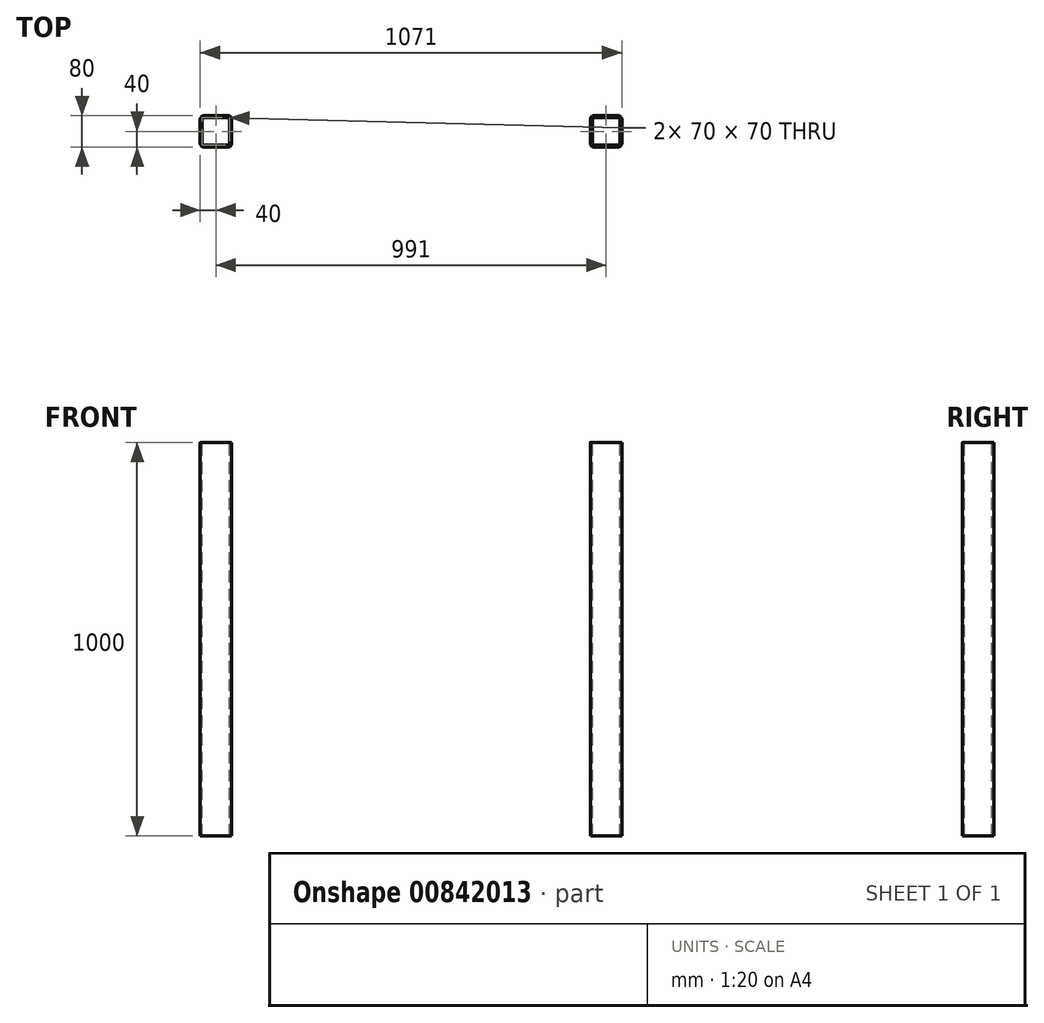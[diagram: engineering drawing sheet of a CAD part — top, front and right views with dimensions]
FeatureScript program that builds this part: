
annotation { "Feature Type Name" : "Feature", "Feature Type Description" : "" }
export const myFeature = defineFeature(function(context is Context, id is Id, definition is map)
    precondition{}
    {
        {
            var Q0;
            Q0=qCreatedBy(makeId("Top.planeOp"),FACE);
            var sketch = newSketch(context, id + "F0", { "sketchPlane" : qUnion([Q0])});
            skLineSegment(sketch, "E0.bottom", {"start": v(-500, 275) * mm, "end": v(500, 275) * mm, "construction": true});
            skLineSegment(sketch, "E0.top", {"start": v(-500, -275) * mm, "end": v(500, -275) * mm, "construction": true});
            skLineSegment(sketch, "E0.left", {"start": v(-500, 275) * mm, "end": v(-500, -275) * mm, "construction": true});
            skLineSegment(sketch, "E0.right", {"start": v(500, 275) * mm, "end": v(500, -275) * mm, "construction": true});
            skPoint(sketch, "E0.middle", {"position": v(0, 0) * mm});
            skLineSegment(sketch, "E1.bottom", {"start": v(-530, 315) * mm, "end": v(-470, 315) * mm});
            skLineSegment(sketch, "E1.top", {"start": v(-530, 235) * mm, "end": v(-470, 235) * mm});
            skLineSegment(sketch, "E1.left", {"start": v(-540, 305) * mm, "end": v(-540, 245) * mm});
            skLineSegment(sketch, "E1.right", {"start": v(-460, 305) * mm, "end": v(-460, 245) * mm});
            skPoint(sketch, "E1.middle", {"position": v(-500, 275) * mm});
            skLineSegment(sketch, "E2.bottom", {"start": v(-535, 310) * mm, "end": v(-465, 310) * mm});
            skLineSegment(sketch, "E2.top", {"start": v(-535, 240) * mm, "end": v(-465, 240) * mm});
            skLineSegment(sketch, "E2.left", {"start": v(-535, 310) * mm, "end": v(-535, 240) * mm});
            skLineSegment(sketch, "E2.right", {"start": v(-465, 310) * mm, "end": v(-465, 240) * mm});
            skPoint(sketch, "E3.visualSharp", {"position": v(-540, 315) * mm});
            skArc(sketch, "E3.filletArc", {"start": v(-530, 315) * mm, "mid": v(-537.07, 312.07) * mm, "end": v(-540, 305) * mm});
            skPoint(sketch, "E4.visualSharp", {"position": v(-460, 315) * mm});
            skArc(sketch, "E4.filletArc", {"start": v(-460, 305) * mm, "mid": v(-462.93, 312.07) * mm, "end": v(-470, 315) * mm});
            skPoint(sketch, "E5.visualSharp", {"position": v(-460, 235) * mm});
            skArc(sketch, "E5.filletArc", {"start": v(-470, 235) * mm, "mid": v(-462.93, 237.93) * mm, "end": v(-460, 245) * mm});
            skPoint(sketch, "E6.visualSharp", {"position": v(-540, 235) * mm});
            skArc(sketch, "E6.filletArc", {"start": v(-540, 245) * mm, "mid": v(-537.07, 237.93) * mm, "end": v(-530, 235) * mm});
            skLineSegment(sketch, "E7.bottom", {"start": v(461, 315) * mm, "end": v(521, 315) * mm});
            skLineSegment(sketch, "E7.top", {"start": v(461, 235) * mm, "end": v(521, 235) * mm});
            skLineSegment(sketch, "E7.left", {"start": v(451, 305) * mm, "end": v(451, 245) * mm});
            skLineSegment(sketch, "E7.right", {"start": v(531, 305) * mm, "end": v(531, 245) * mm});
            skPoint(sketch, "E7.middle", {"position": v(491, 275) * mm});
            skLineSegment(sketch, "E8.bottom", {"start": v(456, 310) * mm, "end": v(526, 310) * mm});
            skLineSegment(sketch, "E8.top", {"start": v(456, 240) * mm, "end": v(526, 240) * mm});
            skLineSegment(sketch, "E8.left", {"start": v(456, 310) * mm, "end": v(456, 240) * mm});
            skLineSegment(sketch, "E8.right", {"start": v(526, 310) * mm, "end": v(526, 240) * mm});
            skPoint(sketch, "E9.visualSharp", {"position": v(451, 315) * mm});
            skArc(sketch, "E9.filletArc", {"start": v(461, 315) * mm, "mid": v(453.93, 312.07) * mm, "end": v(451, 305) * mm});
            skPoint(sketch, "E10.visualSharp", {"position": v(531, 315) * mm});
            skArc(sketch, "E10.filletArc", {"start": v(531, 305) * mm, "mid": v(528.07, 312.07) * mm, "end": v(521, 315) * mm});
            skPoint(sketch, "E11.visualSharp", {"position": v(531, 235) * mm});
            skArc(sketch, "E11.filletArc", {"start": v(521, 235) * mm, "mid": v(528.07, 237.93) * mm, "end": v(531, 245) * mm});
            skPoint(sketch, "E12.visualSharp", {"position": v(451, 235) * mm});
            skArc(sketch, "E12.filletArc", {"start": v(451, 245) * mm, "mid": v(453.93, 237.93) * mm, "end": v(461, 235) * mm});
            skSolve(sketch);
        }
        {
            var Q0;
            Q0=makeQuery(id+"F0.imprint","IMPRINT",FACE,{"disambiguationData":[TD([[makeQuery(id+"F0.imprint","IMPRINT",EDGE,{"derivedFrom":sQuery(id+"F0.wireOp",EDGE,"E1.bottom")}),-1.0]])]});
            var Q1;
            Q1=makeQuery(id+"F0.imprint","IMPRINT",FACE,{"disambiguationData":[TD([[makeQuery(id+"F0.imprint","IMPRINT",EDGE,{"derivedFrom":sQuery(id+"F0.wireOp",EDGE,"E7.bottom")}),-1.0]])]});
            extrude(context, id + "F1", {"entities" : qUnion([Q0, Q1]), "oppositeDirection" : true, "depth" : 1000 * mm, "offsetDistance" : 25 * mm});
        }
    });
